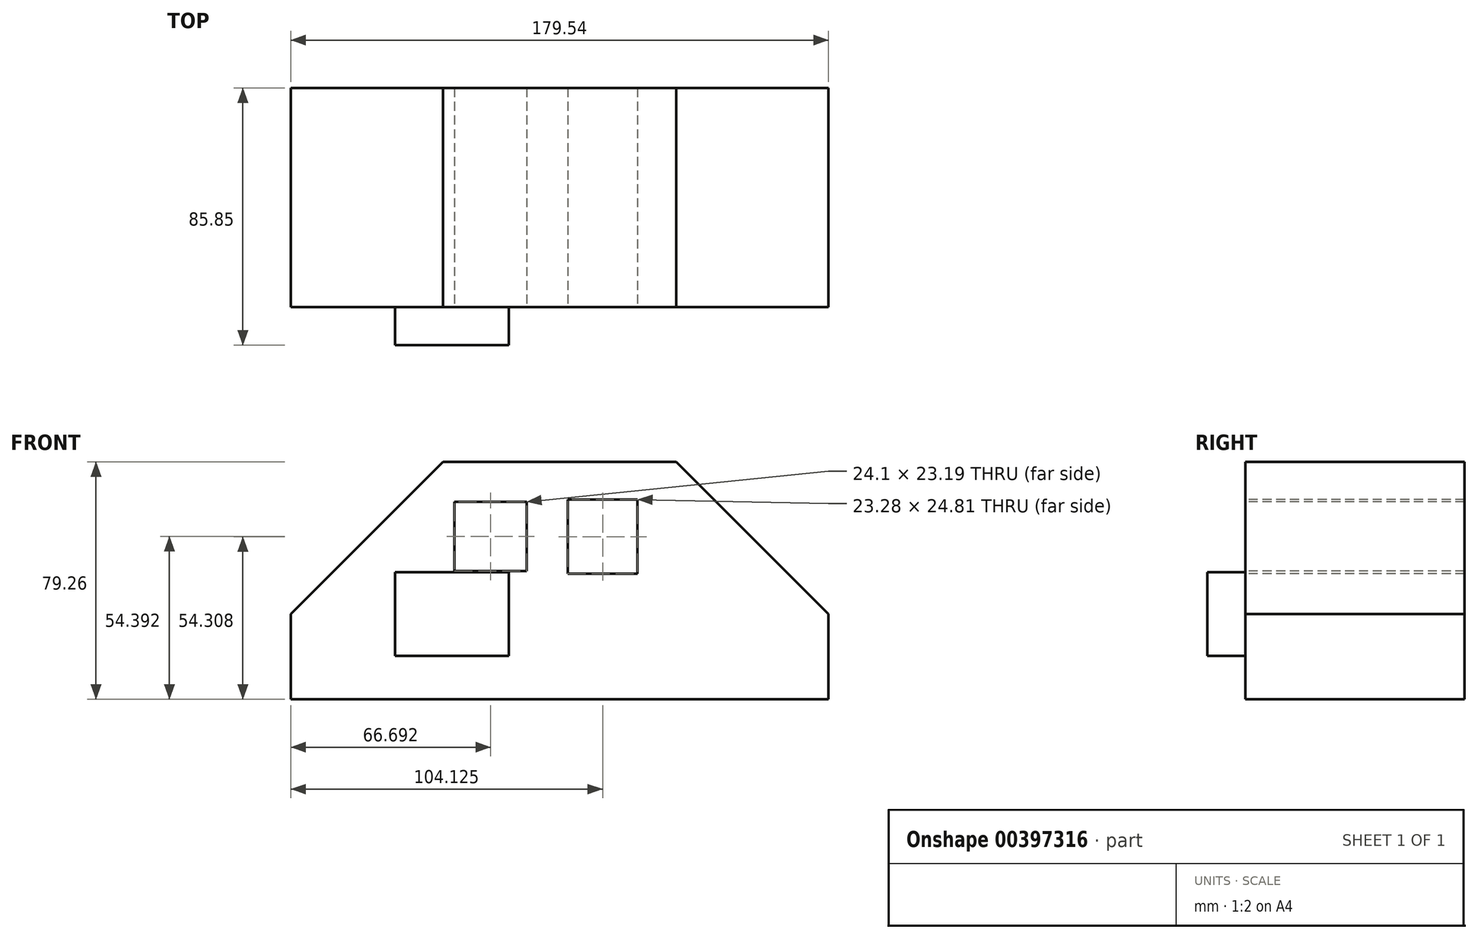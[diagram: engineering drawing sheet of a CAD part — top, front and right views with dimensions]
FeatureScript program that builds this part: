
annotation { "Feature Type Name" : "Feature", "Feature Type Description" : "" }
export const myFeature = defineFeature(function(context is Context, id is Id, definition is map)
    precondition{}
    {
        {
            var Q0;
            Q0=qCreatedBy(makeId("Front.planeOp"),FACE);
            var sketch = newSketch(context, id + "F0", { "sketchPlane" : qUnion([Q0])});
            skLineSegment(sketch, "E0.bottom", {"start": v(-84.7, 47.67) * mm, "end": v(94.84, 47.67) * mm});
            skLineSegment(sketch, "E0.top", {"start": v(-84.7, -31.6) * mm, "end": v(94.84, -31.6) * mm});
            skLineSegment(sketch, "E0.left", {"start": v(-84.7, 47.67) * mm, "end": v(-84.7, -31.6) * mm});
            skLineSegment(sketch, "E0.right", {"start": v(94.84, 47.67) * mm, "end": v(94.84, -31.6) * mm});
            skSolve(sketch);
        }
        {
            var Q0;
            Q0 = qSketchRegion(id + "F0", true);
            extrude(context, id + "F1", {"entities" : qUnion([Q0]), "depth" : 73.15 * mm});
        }
        {
            var Q0;
            Q0=makeQuery(id+"F1.opExtrude","SWEPT_EDGE",EDGE,{"disambiguationData":[OSD([sQuery(id+"F0.wireOp",EDGE,"E0.bottom"),sQuery(id+"F0.wireOp",EDGE,"E0.left")])]});
            chamfer(context, id + "F2", {"entities" : qUnion([Q0]), "width" : 50.8 * mm, "tangentPropagation" : true});
        }
        {
            var Q0;
            Q0=makeQuery(id+"F1.opExtrude","CAP_FACE",FACE,{"disambiguationData":[OSD([sQuery(id+"F0.wireOp",EDGE,"E0.bottom"),sQuery(id+"F0.wireOp",EDGE,"E0.top"),sQuery(id+"F0.wireOp",EDGE,"E0.left"),sQuery(id+"F0.wireOp",EDGE,"E0.right")])],"isStart":false});
            var sketch = newSketch(context, id + "F3", { "sketchPlane" : qUnion([Q0])});
            skLineSegment(sketch, "E1.bottom", {"start": v(-30.06, 34.4) * mm, "end": v(-5.96, 34.4) * mm});
            skLineSegment(sketch, "E1.top", {"start": v(-30.06, 11.2) * mm, "end": v(-5.96, 11.2) * mm});
            skLineSegment(sketch, "E1.left", {"start": v(-30.06, 34.4) * mm, "end": v(-30.06, 11.2) * mm});
            skLineSegment(sketch, "E1.right", {"start": v(-5.96, 34.4) * mm, "end": v(-5.96, 11.2) * mm});
            skSolve(sketch);
        }
        {
            var Q0;
            Q0 = qSketchRegion(id + "F3", true);
            extrude(context, id + "F4", {"entities" : qUnion([Q0]), "operationType" : NewBodyOperationType.REMOVE, "oppositeDirection" : true, "depth" : 286 * mm});
        }
        {
            var Q0;
            Q0=makeQuery(id+"F1.opExtrude","CAP_FACE",FACE,{"disambiguationData":[OSD([sQuery(id+"F0.wireOp",EDGE,"E0.bottom"),sQuery(id+"F0.wireOp",EDGE,"E0.top"),sQuery(id+"F0.wireOp",EDGE,"E0.left"),sQuery(id+"F0.wireOp",EDGE,"E0.right")])],"isStart":false});
            var sketch = newSketch(context, id + "F5", { "sketchPlane" : qUnion([Q0])});
            skLineSegment(sketch, "E2.bottom", {"start": v(7.78, 35.12) * mm, "end": v(31.07, 35.12) * mm});
            skLineSegment(sketch, "E2.top", {"start": v(7.78, 10.31) * mm, "end": v(31.07, 10.31) * mm});
            skLineSegment(sketch, "E2.left", {"start": v(7.78, 35.12) * mm, "end": v(7.78, 10.31) * mm});
            skLineSegment(sketch, "E2.right", {"start": v(31.07, 35.12) * mm, "end": v(31.07, 10.31) * mm});
            skSolve(sketch);
        }
        {
            var Q0;
            Q0 = qSketchRegion(id + "F5", true);
            extrude(context, id + "F6", {"entities" : qUnion([Q0]), "operationType" : NewBodyOperationType.REMOVE, "oppositeDirection" : true, "depth" : 221.74 * mm});
        }
        {
            var Q0;
            Q0=makeQuery(id+"F1.opExtrude","SWEPT_EDGE",EDGE,{"disambiguationData":[OSD([sQuery(id+"F0.wireOp",EDGE,"E0.bottom"),sQuery(id+"F0.wireOp",EDGE,"E0.right")])]});
            chamfer(context, id + "F7", {"entities" : qUnion([Q0]), "width" : 50.8 * mm, "tangentPropagation" : true});
        }
        {
            var Q0;
            Q0=makeQuery(id+"F1.opExtrude","CAP_FACE",FACE,{"disambiguationData":[OSD([sQuery(id+"F0.wireOp",EDGE,"E0.bottom"),sQuery(id+"F0.wireOp",EDGE,"E0.top"),sQuery(id+"F0.wireOp",EDGE,"E0.left"),sQuery(id+"F0.wireOp",EDGE,"E0.right")])],"isStart":false});
            var sketch = newSketch(context, id + "F8", { "sketchPlane" : qUnion([Q0])});
            skLineSegment(sketch, "E3.bottom", {"start": v(-49.93, 10.8) * mm, "end": v(-11.83, 10.8) * mm});
            skLineSegment(sketch, "E3.top", {"start": v(-49.93, -17.15) * mm, "end": v(-11.83, -17.15) * mm});
            skLineSegment(sketch, "E3.left", {"start": v(-49.93, 10.8) * mm, "end": v(-49.93, -17.15) * mm});
            skLineSegment(sketch, "E3.right", {"start": v(-11.83, 10.8) * mm, "end": v(-11.83, -17.15) * mm});
            skSolve(sketch);
        }
        {
            var Q0;
            Q0 = qSketchRegion(id + "F8", true);
            extrude(context, id + "F9", {"entities" : qUnion([Q0]), "operationType" : NewBodyOperationType.ADD, "depth" : 12.7 * mm});
        }
    });
